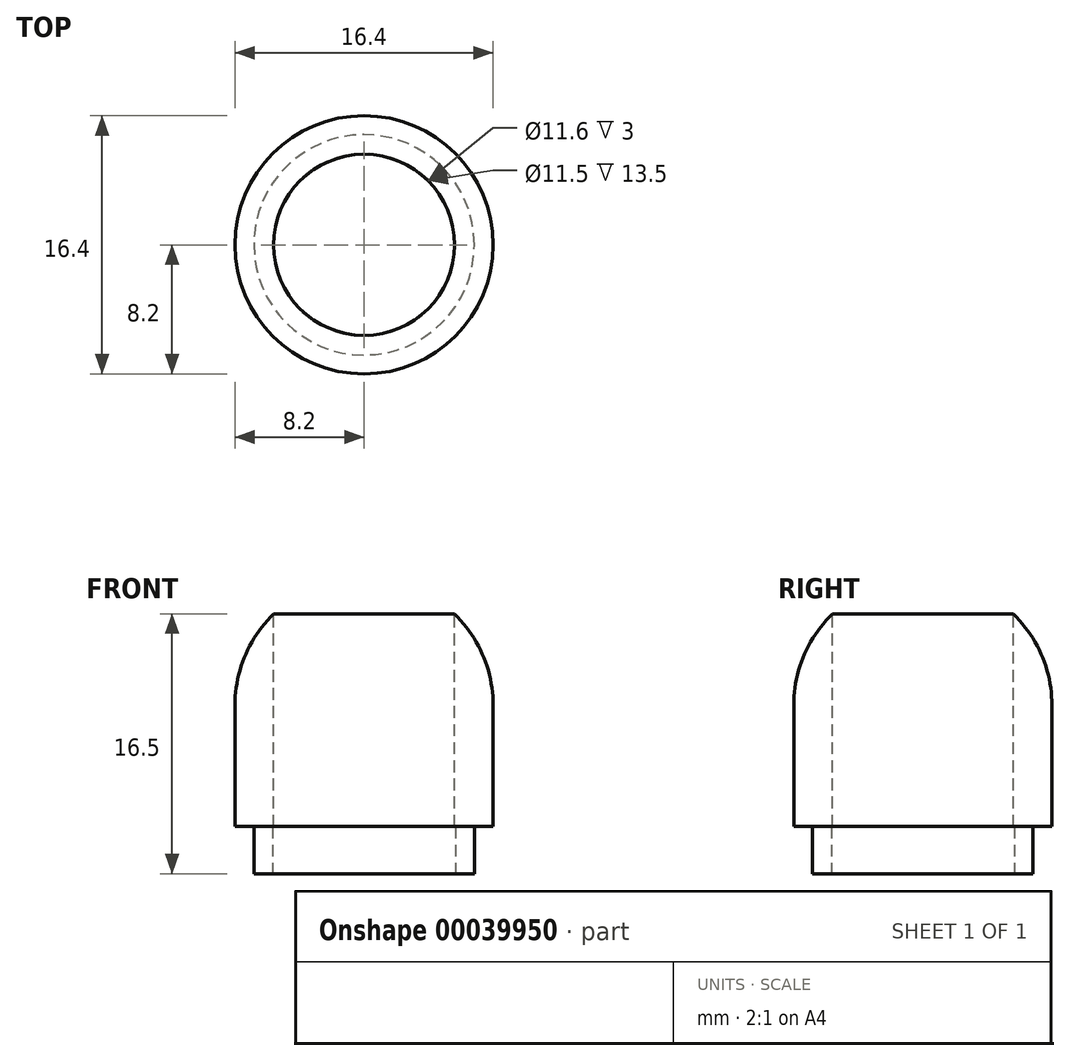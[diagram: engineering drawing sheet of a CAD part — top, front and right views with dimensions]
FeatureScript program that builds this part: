
annotation { "Feature Type Name" : "Feature", "Feature Type Description" : "" }
export const myFeature = defineFeature(function(context is Context, id is Id, definition is map)
    precondition{}
    {
        {
            var Q0;
            Q0=qCreatedBy(makeId("Top.planeOp"),FACE);
            var sketch = newSketch(context, id + "F0", { "sketchPlane" : qUnion([Q0])});
            skCircle(sketch, "E0", {"center": v(0, 0) * mm, "radius": 7 * mm});
            skCircle(sketch, "E1", {"center": v(0, 0) * mm, "radius": 5.8 * mm});
            skSolve(sketch);
        }
        {
            var Q0;
            Q0 = qSketchRegion(id + "F0", true);
            extrude(context, id + "F1", {"entities" : qUnion([Q0]), "depth" : 3 * mm});
        }
        {
            var Q0;
            Q0=makeQuery(id+"F1.opExtrude","CAP_FACE",FACE,{"disambiguationData":[OSD([sQuery(id+"F0.wireOp",EDGE,"E0"),sQuery(id+"F0.wireOp",EDGE,"E1")])],"isStart":false});
            var sketch = newSketch(context, id + "F2", { "sketchPlane" : qUnion([Q0])});
            skCircle(sketch, "E2", {"center": v(0, 0) * mm, "radius": 8.2 * mm});
            skSolve(sketch);
        }
        {
            var Q0;
            Q0 = qSketchRegion(id + "F2", true);
            extrude(context, id + "F3", {"entities" : qUnion([Q0]), "operationType" : NewBodyOperationType.ADD, "depth" : 13.5 * mm});
        }
        {
            var Q0;
            Q0=makeQuery(id+"F3.opExtrude","CAP_FACE",FACE,{"disambiguationData":[OSD([sQuery(id+"F2.wireOp",EDGE,"E2")])],"isStart":false});
            var sketch = newSketch(context, id + "F4", { "sketchPlane" : qUnion([Q0])});
            skCircle(sketch, "E3", {"center": v(0, 0) * mm, "radius": 5.75 * mm});
            skSolve(sketch);
        }
        {
            var Q0;
            Q0 = qSketchRegion(id + "F4", true);
            extrude(context, id + "F5", {"entities" : qUnion([Q0]), "operationType" : NewBodyOperationType.REMOVE, "endBound" : BoundingType.THROUGH_ALL, "oppositeDirection" : true, "depth" : 25 * mm});
        }
        {
            var Q0;
            Q0=makeQuery(id+"F3.opExtrude","CAP_EDGE",EDGE,{"disambiguationData":[OSD([sQuery(id+"F2.wireOp",EDGE,"E2")])],"isStart":false});
            fillet(context, id + "F6", {"entities" : qUnion([Q0]), "radius" : 8.1 * mm, "tangentPropagation" : true, "allowEdgeOverflow" : false});
        }
    });
